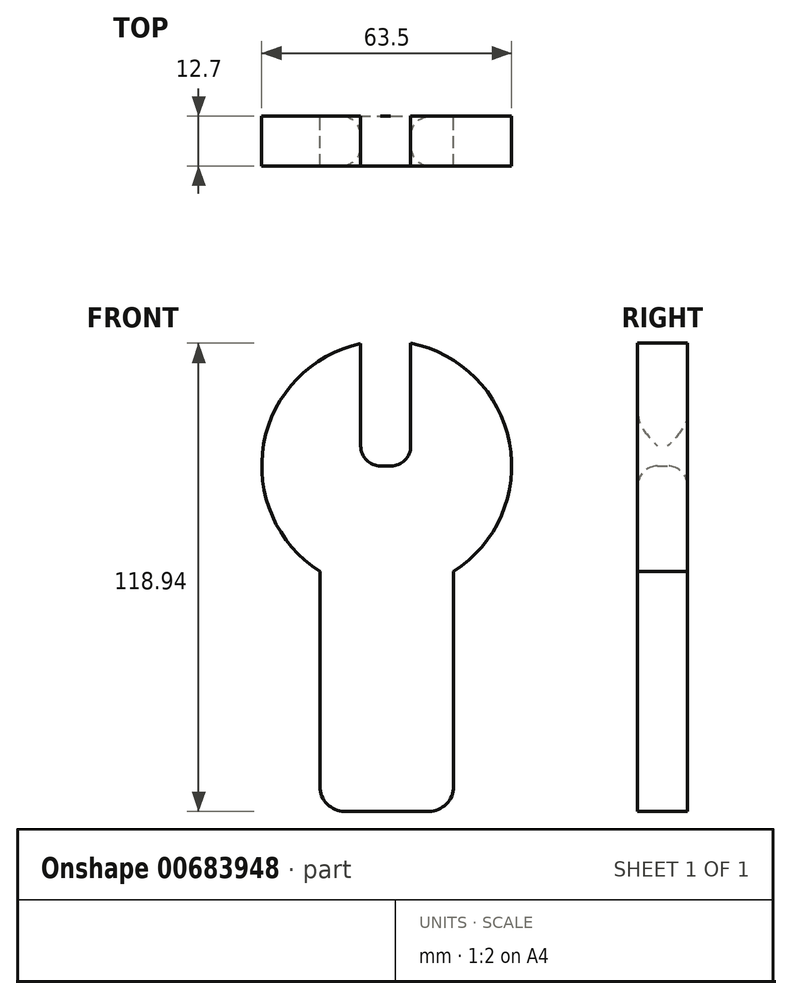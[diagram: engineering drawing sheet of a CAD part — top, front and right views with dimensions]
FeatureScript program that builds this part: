
annotation { "Feature Type Name" : "Feature", "Feature Type Description" : "" }
export const myFeature = defineFeature(function(context is Context, id is Id, definition is map)
    precondition{}
    {
        {
            var Q0;
            Q0=qCreatedBy(makeId("Front.planeOp"),FACE);
            var sketch = newSketch(context, id + "F0", { "sketchPlane" : qUnion([Q0])});
            skLineSegment(sketch, "E0.bottom", {"start": v(-17.01, 17) * mm, "end": v(17.01, 17) * mm});
            skLineSegment(sketch, "E0.top", {"start": v(-10.66, -43.97) * mm, "end": v(10.66, -43.97) * mm});
            skLineSegment(sketch, "E0.left", {"start": v(-17.01, 17) * mm, "end": v(-17.01, -37.62) * mm});
            skLineSegment(sketch, "E0.right", {"start": v(17.01, 17) * mm, "end": v(17.01, -37.62) * mm});
            skPoint(sketch, "E1.visualSharp", {"position": v(-17.01, -43.97) * mm});
            skArc(sketch, "E1.filletArc", {"start": v(-17.01, -37.62) * mm, "mid": v(-15.15, -42.1) * mm, "end": v(-10.66, -43.97) * mm});
            skPoint(sketch, "E2.visualSharp", {"position": v(17.01, -43.97) * mm});
            skArc(sketch, "E2.filletArc", {"start": v(10.66, -43.97) * mm, "mid": v(15.15, -42.1) * mm, "end": v(17.01, -37.62) * mm});
            skCircle(sketch, "E3", {"center": v(0, 43.8) * mm, "radius": 31.75 * mm});
            skPoint(sketch, "E3.third.point", {"position": v(30.3, 53.27) * mm});
            skLineSegment(sketch, "E4.top", {"start": v(6.1, 43.76) * mm, "end": v(-6.6, 43.76) * mm});
            skLineSegment(sketch, "E4.left", {"start": v(6.1, 62.47) * mm, "end": v(6.1, 43.76) * mm});
            skLineSegment(sketch, "E4.right", {"start": v(-6.6, 62.47) * mm, "end": v(-6.6, 43.76) * mm});
            skPoint(sketch, "E4.middle", {"position": v(0, 65.56) * mm});
            skLineSegment(sketch, "E5", {"start": v(-6.6, 62.47) * mm, "end": v(-6.6, 74.87) * mm});
            skLineSegment(sketch, "E6", {"start": v(6.1, 62.47) * mm, "end": v(6.1, 74.97) * mm});
            skSolve(sketch);
        }
        {
            var Q0;
            {var subQ0=sQuery(id+"F0.wireOp",EDGE,"5f5yoJOe-R2SZ-vWBl-2VqM-NOOLHwAG60Jt.top");Q0=makeQuery(id+"F0.imprint","IMPRINT",FACE,{"disambiguationData":[TD([[makeQuery(id+"F0.imprint","IMPRINT",EDGE,{"derivedFrom":subQ0}),-1.0]])]});}
            var Q1;
            {var subQ0=sQuery(id+"F0.wireOp",EDGE,"g1K7diLN-VQJg-0hxA-TzyU-W1L6Z0WY6TER");var subQ1=sQuery(id+"F0.wireOp",EDGE,"E0.bottom");var subQ3=makeQuery(id+"F0.imprint","INTERSECT",VERTEX,{"derivedFrom":[subQ1,subQ0]});Q1=makeQuery(id+"F0.imprint","IMPRINT",FACE,{"disambiguationData":[TD([[makeQuery(id+"F0.imprint","IMPRINT",EDGE,{"disambiguationData":[TD([[subQ3,-1.0]])],"derivedFrom":subQ1}),-1.0]])]});}
            var Q2;
            Q2=makeQuery(id+"F0.imprint","IMPRINT",FACE,{"disambiguationData":[TD([[makeQuery(id+"F0.imprint","IMPRINT",EDGE,{"derivedFrom":sQuery(id+"F0.wireOp",EDGE,"E0.top")}),1.0]])]});
            var Q3;
            {var subQ1=sQuery(id+"F0.wireOp",EDGE,"E0.bottom");Q3=makeQuery(id+"F0.imprint","IMPRINT",FACE,{"disambiguationData":[TD([[makeQuery(id+"F0.imprint","IMPRINT",EDGE,{"derivedFrom":subQ1}),1.0]])]});}
            extrude(context, id + "F1", {"entities" : qUnion([Q0, Q1, Q2, Q3]), "depth" : 12.7 * mm, "offsetDistance" : 25.4 * mm});
        }
        {
            var Q0;
            Q0=makeQuery(id+"F1.opExtrude","SWEPT_FACE",FACE,{"disambiguationData":[OSD([sQuery(id+"F0.wireOp",EDGE,"E4.top")])]});
            fillet(context, id + "F2", {"entities" : qUnion([Q0]), "radius" : 5.08 * mm, "tangentPropagation" : true, "allowEdgeOverflow" : false});
        }
    });
